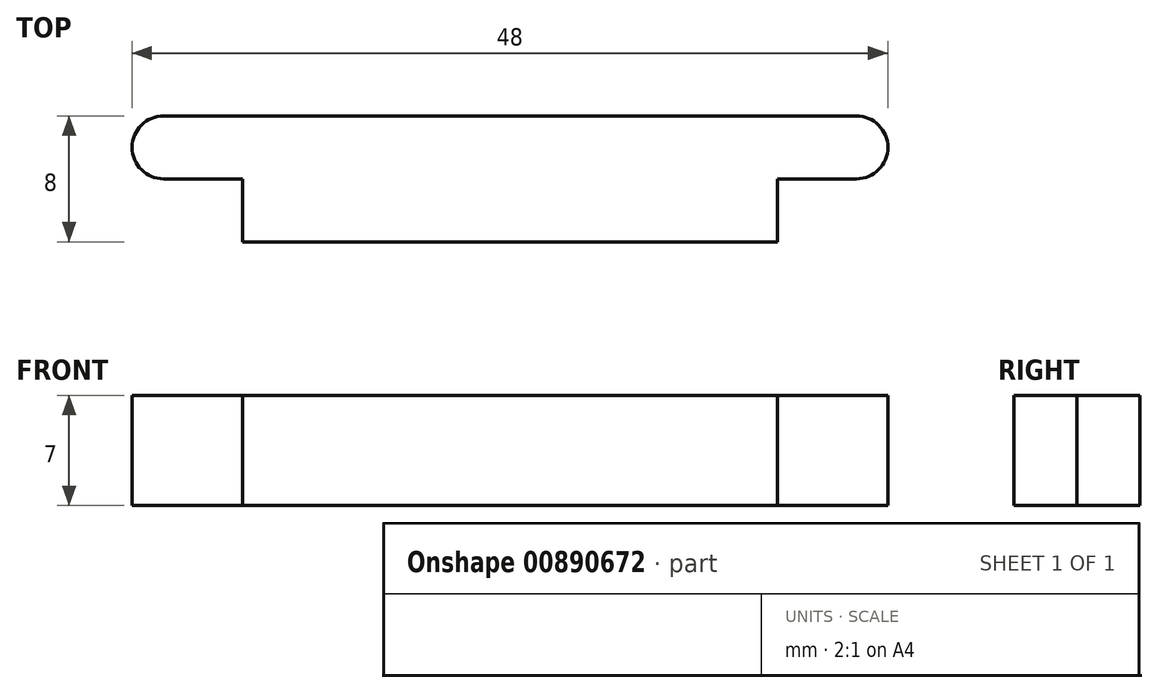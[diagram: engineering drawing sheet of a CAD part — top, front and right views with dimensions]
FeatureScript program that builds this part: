
annotation { "Feature Type Name" : "Feature", "Feature Type Description" : "" }
export const myFeature = defineFeature(function(context is Context, id is Id, definition is map)
    precondition{}
    {
        {
            var Q0;
            Q0=qCreatedBy(makeId("Top.planeOp"),FACE);
            var sketch = newSketch(context, id + "F0", { "sketchPlane" : qUnion([Q0])});
            skLineSegment(sketch, "E0.bottom", {"start": v(0, 0) * mm, "end": v(48, 0) * mm});
            skLineSegment(sketch, "E0.top", {"start": v(0, -4) * mm, "end": v(48, -4) * mm});
            skLineSegment(sketch, "E0.left", {"start": v(0, 0) * mm, "end": v(0, -4) * mm});
            skLineSegment(sketch, "E0.right", {"start": v(48, 0) * mm, "end": v(48, -4) * mm});
            skLineSegment(sketch, "E1.bottom", {"start": v(7, -4) * mm, "end": v(41, -4) * mm});
            skLineSegment(sketch, "E1.top", {"start": v(7, -8) * mm, "end": v(41, -8) * mm});
            skLineSegment(sketch, "E1.left", {"start": v(7, -4) * mm, "end": v(7, -8) * mm});
            skLineSegment(sketch, "E1.right", {"start": v(41, -4) * mm, "end": v(41, -8) * mm});
            skSolve(sketch);
        }
        {
            var Q0;
            Q0=makeQuery(id+"F0.imprint","IMPRINT",FACE,{"disambiguationData":[TD([[makeQuery(id+"F0.imprint","IMPRINT",EDGE,{"derivedFrom":sQuery(id+"F0.wireOp",EDGE,"E0.bottom")}),-1.0]])]});
            var Q1;
            Q1=makeQuery(id+"F0.imprint","IMPRINT",FACE,{"disambiguationData":[TD([[makeQuery(id+"F0.imprint","IMPRINT",EDGE,{"derivedFrom":sQuery(id+"F0.wireOp",EDGE,"E1.top")}),1.0]])]});
            extrude(context, id + "F1", {"entities" : qUnion([Q0, Q1]), "depth" : 7 * mm, "offsetDistance" : 25 * mm});
        }
        {
            var Q0;
            Q0=makeQuery(id+"F1.opExtrude","SWEPT_EDGE",EDGE,{"disambiguationData":[OSD([sQuery(id+"F0.wireOp",EDGE,"E0.top"),sQuery(id+"F0.wireOp",EDGE,"E0.right")])]});
            var Q1;
            Q1=makeQuery(id+"F1.opExtrude","SWEPT_EDGE",EDGE,{"disambiguationData":[OSD([sQuery(id+"F0.wireOp",EDGE,"E0.bottom"),sQuery(id+"F0.wireOp",EDGE,"E0.right")])]});
            var Q2;
            Q2=makeQuery(id+"F1.opExtrude","SWEPT_EDGE",EDGE,{"disambiguationData":[OSD([sQuery(id+"F0.wireOp",EDGE,"E0.top"),sQuery(id+"F0.wireOp",EDGE,"E0.left")])]});
            var Q3;
            Q3=makeQuery(id+"F1.opExtrude","SWEPT_EDGE",EDGE,{"disambiguationData":[OSD([sQuery(id+"F0.wireOp",EDGE,"E0.bottom"),sQuery(id+"F0.wireOp",EDGE,"E0.left")])]});
            fillet(context, id + "F2", {"entities" : qUnion([Q0, Q1, Q2, Q3]), "radius" : 2 * mm, "tangentPropagation" : true, "allowEdgeOverflow" : false});
        }
    });
